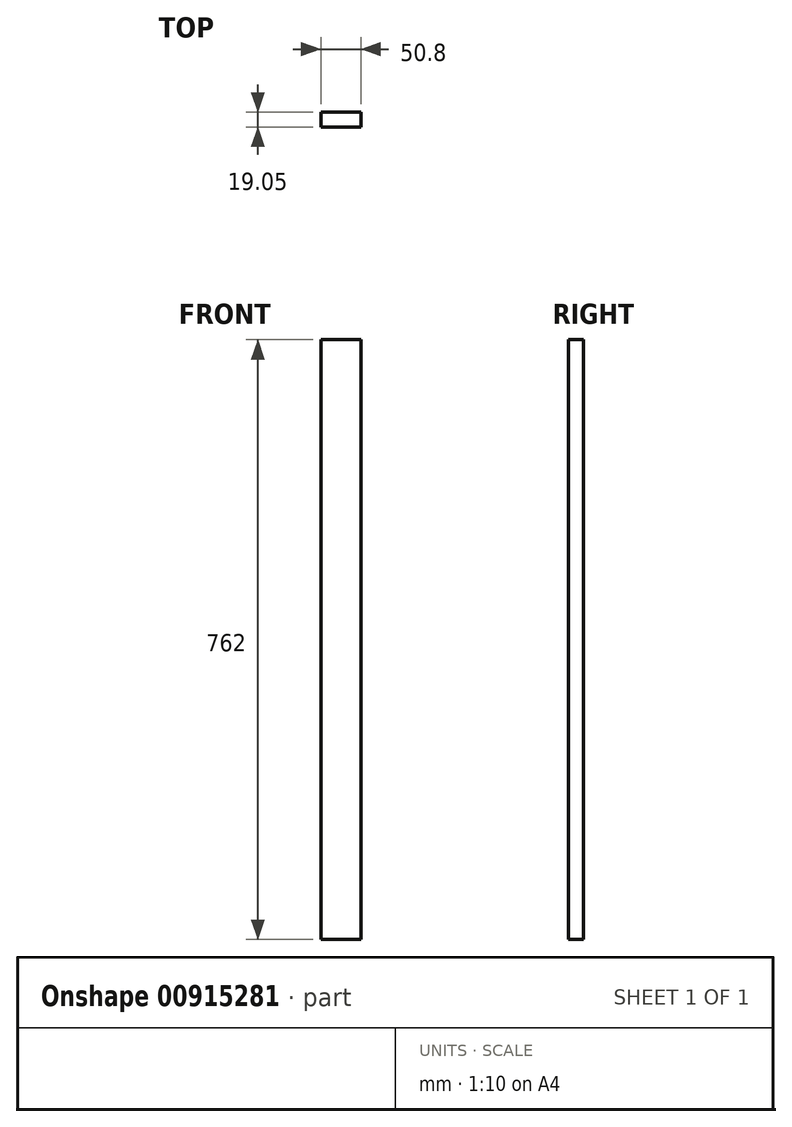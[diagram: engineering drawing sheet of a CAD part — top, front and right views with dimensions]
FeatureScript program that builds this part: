
annotation { "Feature Type Name" : "Feature", "Feature Type Description" : "" }
export const myFeature = defineFeature(function(context is Context, id is Id, definition is map)
    precondition{}
    {
        {
            var Q0;
            Q0=qCreatedBy(makeId("Front.planeOp"),FACE);
            var sketch = newSketch(context, id + "F0", { "sketchPlane" : qUnion([Q0])});
            skLineSegment(sketch, "E0.bottom", {"start": v(25.4, 381) * mm, "end": v(-25.4, 381) * mm});
            skLineSegment(sketch, "E0.top", {"start": v(25.4, -381) * mm, "end": v(-25.4, -381) * mm});
            skLineSegment(sketch, "E0.left", {"start": v(25.4, 381) * mm, "end": v(25.4, -381) * mm});
            skLineSegment(sketch, "E0.right", {"start": v(-25.4, 381) * mm, "end": v(-25.4, -381) * mm});
            skPoint(sketch, "E0.middle", {"position": v(0, 0) * mm});
            skSolve(sketch);
        }
        {
            var Q0;
            Q0=makeQuery(id+"F0.imprint","IMPRINT",FACE,{"disambiguationData":[TD([[makeQuery(id+"F0.imprint","IMPRINT",EDGE,{"derivedFrom":sQuery(id+"F0.wireOp",EDGE,"E0.bottom")}),1.0]])]});
            extrude(context, id + "F1", {"entities" : qUnion([Q0]), "depth" : 19.05 * mm, "offsetDistance" : 25.4 * mm});
        }
    });
